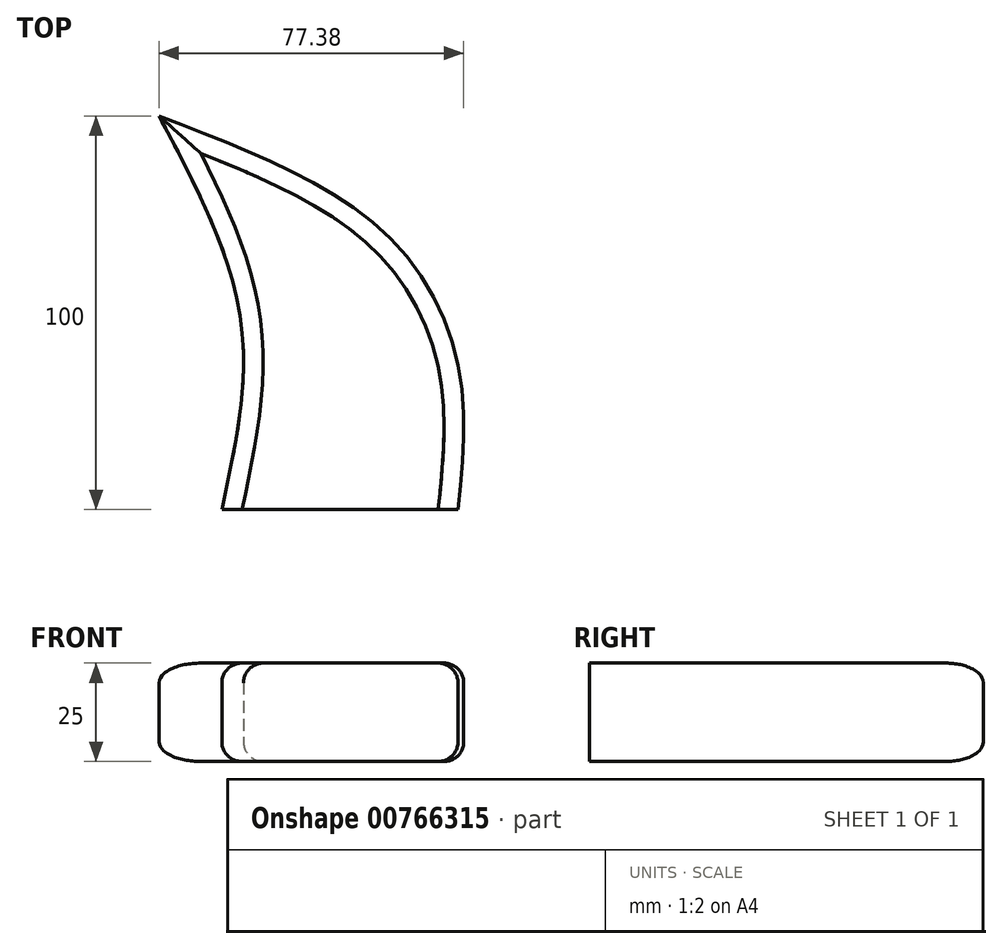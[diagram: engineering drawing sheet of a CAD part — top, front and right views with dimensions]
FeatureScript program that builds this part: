
annotation { "Feature Type Name" : "Feature", "Feature Type Description" : "" }
export const myFeature = defineFeature(function(context is Context, id is Id, definition is map)
    precondition{}
    {
        {
            var Q0;
            Q0=qCreatedBy(makeId("Top.planeOp"),FACE);
            var sketch = newSketch(context, id + "F0", { "sketchPlane" : qUnion([Q0])});
            skLineSegment(sketch, "E0", {"start": v(-69.29, -10.66) * mm, "end": v(-9.29, -10.66) * mm});
            skFitSpline(sketch, "E1", {"points": [v(-9.29, -10.66) * mm, v(-9.29, 26.15) * mm, v(-29.73, 61.32) * mm, v(-85.22, 89.34) * mm], "startDerivative": vector(13.18, 124.4) * mm, "endDerivative": vector(-160.3, 61.82) * mm});
            skFitSpline(sketch, "E2", {"points": [v(-85.22, 89.34) * mm, v(-64.5, 37.68) * mm, v(-69.29, -10.66) * mm], "startDerivative": vector(52.9, -99.87) * mm, "endDerivative": vector(-21.87, -100.14) * mm});
            skSolve(sketch);
        }
        {
            var Q0;
            Q0=makeQuery(id+"F0.imprint","IMPRINT",FACE,{"disambiguationData":[TD([[makeQuery(id+"F0.imprint","IMPRINT",EDGE,{"derivedFrom":sQuery(id+"F0.wireOp",EDGE,"E0")}),1.0]])]});
            extrude(context, id + "F1", {"entities" : qUnion([Q0]), "depth" : 25 * mm, "offsetDistance" : 25 * mm});
        }
        {
            var Q0;
            Q0=makeQuery(id+"F1.opExtrude","CAP_EDGE",EDGE,{"disambiguationData":[OSD([sQuery(id+"F0.wireOp",EDGE,"E1")])],"isStart":true});
            var Q1;
            Q1=makeQuery(id+"F1.opExtrude","CAP_EDGE",EDGE,{"disambiguationData":[OSD([sQuery(id+"F0.wireOp",EDGE,"E1")])],"isStart":false});
            var Q2;
            Q2=makeQuery(id+"F1.opExtrude","CAP_EDGE",EDGE,{"disambiguationData":[OSD([sQuery(id+"F0.wireOp",EDGE,"E2")])],"isStart":false});
            var Q3;
            Q3=makeQuery(id+"F1.opExtrude","CAP_EDGE",EDGE,{"disambiguationData":[OSD([sQuery(id+"F0.wireOp",EDGE,"E2")])],"isStart":true});
            fillet(context, id + "F2", {"entities" : qUnion([Q0, Q1, Q2, Q3]), "radius" : 5 * mm, "tangentPropagation" : true, "allowEdgeOverflow" : false});
        }
    });
